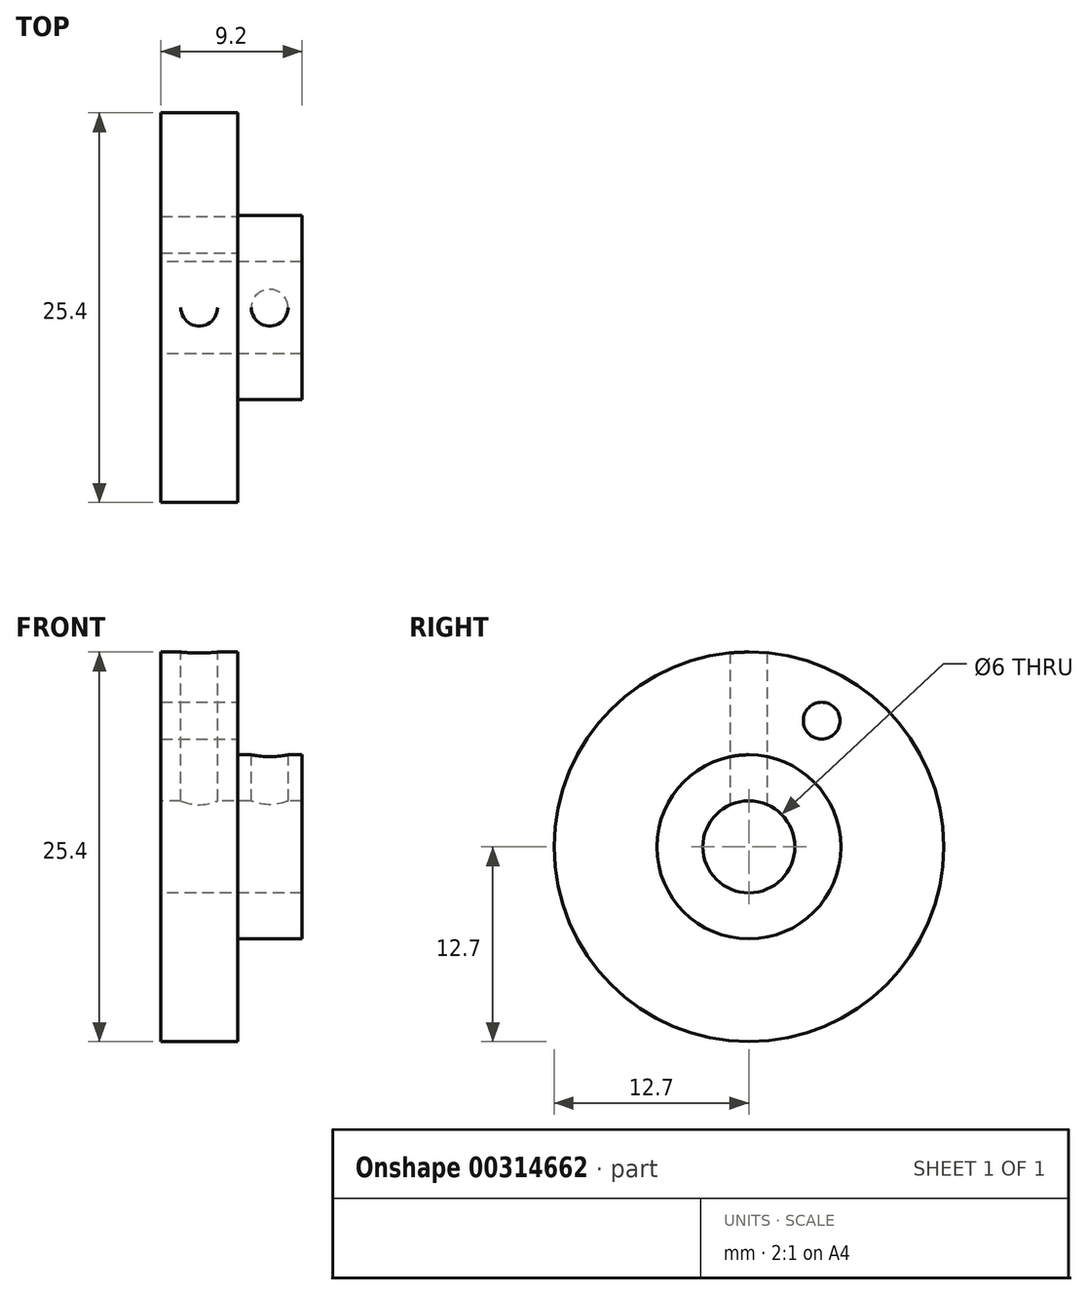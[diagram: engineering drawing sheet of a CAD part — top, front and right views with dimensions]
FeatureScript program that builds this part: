
annotation { "Feature Type Name" : "Feature", "Feature Type Description" : "" }
export const myFeature = defineFeature(function(context is Context, id is Id, definition is map)
    precondition{}
    {
        {
            var Q0;
            Q0=qCreatedBy(makeId("Front.planeOp"),FACE);
            var sketch = newSketch(context, id + "F0", { "sketchPlane" : qUnion([Q0])});
            skLineSegment(sketch, "E0", {"start": v(-2.5, 0) * mm, "end": v(6.7, 0) * mm, "construction": true});
            skLineSegment(sketch, "E1", {"start": v(-2.5, 3) * mm, "end": v(-2.5, 12.7) * mm});
            skLineSegment(sketch, "E2", {"start": v(-2.5, 12.7) * mm, "end": v(2.5, 12.7) * mm});
            skLineSegment(sketch, "E3", {"start": v(2.5, 12.7) * mm, "end": v(2.5, 6) * mm});
            skLineSegment(sketch, "E4", {"start": v(2.5, 6) * mm, "end": v(6.7, 6) * mm});
            skLineSegment(sketch, "E5", {"start": v(6.7, 6) * mm, "end": v(6.7, 3) * mm});
            skLineSegment(sketch, "E6", {"start": v(6.7, 3) * mm, "end": v(-2.5, 3) * mm});
            skPoint(sketch, "E7", {"position": v(0, 12.7) * mm});
            skPoint(sketch, "E8", {"position": v(4.6, 6) * mm});
            skSolve(sketch);
        }
        {
            var Q0;
            Q0 = qSketchRegion(id + "F0", true);
            var Q1;
            Q1=sQuery(id+"F0.wireOp",EDGE,"E0");
            revolve(context, id + "F1", {"entities" : qUnion([Q0]), "axis" : qUnion([Q1]), "revolveType" : RevolveType.FULL});
        }
        {
            var Q0;
            Q0=makeQuery(id+"F1.opRevolve","SWEPT_FACE",FACE,{"disambiguationData":[OSD([sQuery(id+"F0.wireOp",EDGE,"E3")])]});
            var sketch = newSketch(context, id + "F2", { "sketchPlane" : qUnion([Q0])});
            skLineSegment(sketch, "E9", {"start": v(0, 0) * mm, "end": v(4.75, 8.23) * mm, "construction": true});
            skSolve(sketch);
        }
        {
            var Q0;
            Q0=sQuery(id+"F2.wireOp",VERTEX,"E9.end");
            var Q1;
            Q1=makeQuery(id+"F1.opRevolve","SWEPT_BODY",BODY,{"disambiguationData":[OSD([sQuery(id+"F0.wireOp",EDGE,"E1"),sQuery(id+"F0.wireOp",EDGE,"E2"),sQuery(id+"F0.wireOp",EDGE,"E3"),sQuery(id+"F0.wireOp",EDGE,"E4"),sQuery(id+"F0.wireOp",EDGE,"E5"),sQuery(id+"F0.wireOp",EDGE,"E6")])]});
            hole(context, id + "F3", {"style" : HoleStyle.SIMPLE, "endStyle" : HoleEndStyle.THROUGH, "standardTappedOrClearance" : lookupTablePath({ "standard" : "ISO", "engagement" : "75%", "pitch" : "0.6 mm", "size" : "M3", "type" : "Tapped" }), "standardBlindInLast" : lookupTablePath({ "standard" : "ISO", "engagement" : "75%", "pitch" : "0.6 mm", "size" : "M3", "type" : "Tapped" }), "holeDiameter" : 2.4 * mm, "showTappedDepth" : true, "tappedDepth" : 12 * mm, "tapClearance" : 3, "locations" : qUnion([Q0]), "scope" : qUnion([Q1])});
        }
        {
            var Q0;
            Q0=qCreatedBy(makeId("Top.planeOp"),FACE);
            var Q1;
            Q1=sQuery(id+"F0.wireOp",VERTEX,"E7");
            cPlane(context, id + "F4", {"entities" : qUnion([Q0, Q1]), "cplaneType" : CPlaneType.PLANE_POINT, "offset" : 25 * mm, "width" : 150 * mm, "height" : 150 * mm});
        }
        {
            var Q0;
            Q0=qCreatedBy(id+"F4.planeOp",FACE);
            var sketch = newSketch(context, id + "F5", { "sketchPlane" : qUnion([Q0])});
            skPoint(sketch, "E10", {"position": v(0, 0) * mm});
            skSolve(sketch);
        }
        {
            var Q0;
            Q0=sQuery(id+"F5.wireOp",VERTEX,"E10");
            var Q1;
            Q1=makeQuery(id+"F1.opRevolve","SWEPT_BODY",BODY,{"disambiguationData":[OSD([sQuery(id+"F0.wireOp",EDGE,"E1"),sQuery(id+"F0.wireOp",EDGE,"E2"),sQuery(id+"F0.wireOp",EDGE,"E3"),sQuery(id+"F0.wireOp",EDGE,"E4"),sQuery(id+"F0.wireOp",EDGE,"E5"),sQuery(id+"F0.wireOp",EDGE,"E6")])]});
            hole(context, id + "F6", {"style" : HoleStyle.SIMPLE, "endStyle" : HoleEndStyle.BLIND, "standardTappedOrClearance" : lookupTablePath({ "standard" : "ISO", "engagement" : "75%", "pitch" : "0.6 mm", "size" : "M3", "type" : "Tapped" }), "standardBlindInLast" : lookupTablePath({ "standard" : "ISO", "engagement" : "75%", "pitch" : "0.6 mm", "size" : "M3", "type" : "Tapped" }), "holeDiameter" : 2.4 * mm, "showTappedDepth" : true, "holeDepth" : 25.4 / 2 * mm, "tappedDepth" : 10.9 * mm, "tapClearance" : 3, "locations" : qUnion([Q0]), "scope" : qUnion([Q1])});
        }
        {
            var Q0;
            Q0=qCreatedBy(makeId("Top.planeOp"),FACE);
            var Q1;
            Q1=sQuery(id+"F0.wireOp",VERTEX,"E8");
            cPlane(context, id + "F7", {"entities" : qUnion([Q0, Q1]), "cplaneType" : CPlaneType.PLANE_POINT, "offset" : 25 * mm, "width" : 150 * mm, "height" : 150 * mm});
        }
        {
            var Q0;
            Q0=qCreatedBy(id+"F7.planeOp",FACE);
            var sketch = newSketch(context, id + "F8", { "sketchPlane" : qUnion([Q0])});
            skPoint(sketch, "E11", {"position": v(4.6, 0) * mm});
            skSolve(sketch);
        }
        {
            var Q0;
            Q0=sQuery(id+"F8.wireOp",VERTEX,"E11");
            var Q1;
            Q1=makeQuery(id+"F1.opRevolve","SWEPT_BODY",BODY,{"disambiguationData":[OSD([sQuery(id+"F0.wireOp",EDGE,"E1"),sQuery(id+"F0.wireOp",EDGE,"E2"),sQuery(id+"F0.wireOp",EDGE,"E3"),sQuery(id+"F0.wireOp",EDGE,"E4"),sQuery(id+"F0.wireOp",EDGE,"E5"),sQuery(id+"F0.wireOp",EDGE,"E6")])]});
            hole(context, id + "F9", {"style" : HoleStyle.SIMPLE, "endStyle" : HoleEndStyle.BLIND, "standardTappedOrClearance" : lookupTablePath({ "standard" : "ISO", "engagement" : "75%", "pitch" : "0.6 mm", "size" : "M3", "type" : "Tapped" }), "standardBlindInLast" : lookupTablePath({ "standard" : "ISO", "engagement" : "75%", "pitch" : "0.6 mm", "size" : "M3", "type" : "Tapped" }), "holeDiameter" : 2.4 * mm, "showTappedDepth" : true, "holeDepth" : 5 * mm, "tappedDepth" : 3.2 * mm, "tapClearance" : 3, "locations" : qUnion([Q0]), "scope" : qUnion([Q1])});
        }
    });
